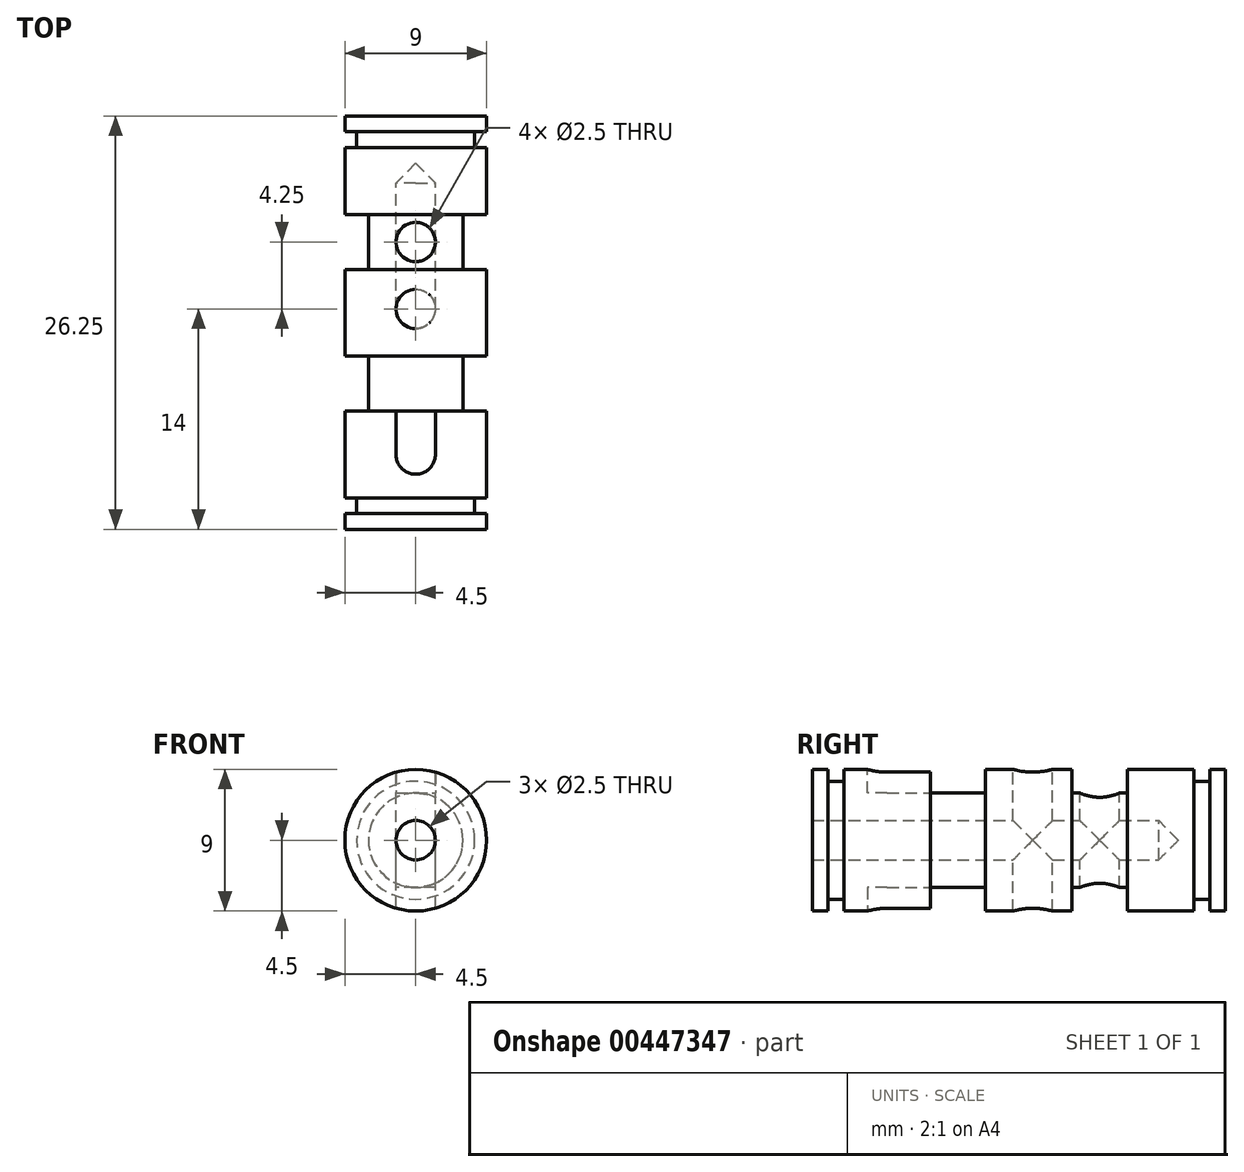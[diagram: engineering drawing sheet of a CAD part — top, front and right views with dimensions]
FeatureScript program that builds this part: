
annotation { "Feature Type Name" : "Feature", "Feature Type Description" : "" }
export const myFeature = defineFeature(function(context is Context, id is Id, definition is map)
    precondition{}
    {
        {
            var Q0;
            Q0=qCreatedBy(makeId("Top.planeOp"),FACE);
            var sketch = newSketch(context, id + "F0", { "sketchPlane" : qUnion([Q0])});
            skLineSegment(sketch, "E0", {"start": v(-2.5, 0) * mm, "end": v(-2.5, 0) * mm});
            skLineSegment(sketch, "E1", {"start": v(-2.5, 0) * mm, "end": v(-1.25, 0) * mm});
            skLineSegment(sketch, "E2", {"start": v(-1.25, 0) * mm, "end": v(-1.25, 22) * mm});
            skLineSegment(sketch, "E3", {"start": v(-1.25, 22) * mm, "end": v(0, 23.25) * mm});
            skLineSegment(sketch, "E4", {"start": v(0, 23.25) * mm, "end": v(0, 26.25) * mm});
            skLineSegment(sketch, "E5", {"start": v(0, 26.25) * mm, "end": v(-4.5, 26.25) * mm});
            skLineSegment(sketch, "E6", {"start": v(-4.5, 26.25) * mm, "end": v(-4.5, 25.25) * mm});
            skLineSegment(sketch, "E7", {"start": v(-4.5, 25.25) * mm, "end": v(-3.75, 25.25) * mm});
            skLineSegment(sketch, "E8", {"start": v(-3.75, 25.25) * mm, "end": v(-3.75, 24.25) * mm});
            skLineSegment(sketch, "E9", {"start": v(-3.75, 24.25) * mm, "end": v(-4.5, 24.25) * mm});
            skLineSegment(sketch, "E10", {"start": v(-4.5, 24.25) * mm, "end": v(-4.5, 20) * mm});
            skLineSegment(sketch, "E11", {"start": v(-4.5, 20) * mm, "end": v(-3, 20) * mm});
            skLineSegment(sketch, "E12", {"start": v(-3, 20) * mm, "end": v(-3, 16.5) * mm});
            skLineSegment(sketch, "E13", {"start": v(-3, 16.5) * mm, "end": v(-4.5, 16.5) * mm});
            skLineSegment(sketch, "E14", {"start": v(-4.5, 16.5) * mm, "end": v(-4.5, 11) * mm});
            skLineSegment(sketch, "E15", {"start": v(-4.5, 11) * mm, "end": v(-3, 11) * mm});
            skLineSegment(sketch, "E16", {"start": v(-3, 11) * mm, "end": v(-3, 7.5) * mm});
            skLineSegment(sketch, "E17", {"start": v(-3, 7.5) * mm, "end": v(-4.5, 7.5) * mm});
            skLineSegment(sketch, "E18", {"start": v(-4.5, 7.5) * mm, "end": v(-4.5, 2) * mm});
            skLineSegment(sketch, "E19", {"start": v(-4.5, 2) * mm, "end": v(-3.75, 2) * mm});
            skLineSegment(sketch, "E20", {"start": v(-3.75, 2) * mm, "end": v(-3.75, 1) * mm});
            skLineSegment(sketch, "E21", {"start": v(-3.75, 1) * mm, "end": v(-4.5, 1) * mm});
            skLineSegment(sketch, "E22", {"start": v(-4.5, 1) * mm, "end": v(-4.5, 0) * mm});
            skLineSegment(sketch, "E23", {"start": v(-4.5, 0) * mm, "end": v(-2.5, 0) * mm});
            skLineSegment(sketch, "E24", {"start": v(0, 9.96) * mm, "end": v(0, -5.2) * mm, "construction": true});
            skLineSegment(sketch, "E25", {"start": v(-3, 9.25) * mm, "end": v(-4.58, 9.25) * mm, "construction": true});
            skPoint(sketch, "E25.endSnap0", {"position": v(-3, 9.25) * mm});
            skLineSegment(sketch, "E26", {"start": v(-3, 18.25) * mm, "end": v(-4.58, 18.25) * mm, "construction": true});
            skLineSegment(sketch, "E27", {"start": v(-4.5, 13.75) * mm, "end": v(-1.25, 13.75) * mm, "construction": true});
            skLineSegment(sketch, "E28", {"start": v(-4.5, 4.75) * mm, "end": v(-1.25, 4.75) * mm, "construction": true});
            skPoint(sketch, "E28.endSnap0", {"position": v(-1.25, 11) * mm});
            skSolve(sketch);
        }
        {
            var Q0;
            Q0=makeQuery(id+"F0.imprint","IMPRINT",FACE,{"disambiguationData":[TD([[makeQuery(id+"F0.imprint","IMPRINT",EDGE,{"derivedFrom":sQuery(id+"F0.wireOp",EDGE,"E1")}),1.0]])]});
            var Q1;
            Q1=sQuery(id+"F0.wireOp",EDGE,"E24");
            revolve(context, id + "F1", {"entities" : qUnion([Q0]), "axis" : qUnion([Q1]), "revolveType" : RevolveType.FULL});
        }
        {
            var Q0;
            Q0=qCreatedBy(makeId("Top.planeOp"),FACE);
            cPlane(context, id + "F2", {"entities" : qUnion([Q0]), "cplaneType" : CPlaneType.OFFSET, "offset" : 4.5 * mm, "width" : 150 * mm, "height" : 150 * mm});
        }
        {
            var Q0;
            Q0=qCreatedBy(id+"F2.planeOp",FACE);
            var sketch = newSketch(context, id + "F3", { "sketchPlane" : qUnion([Q0])});
            skArc(sketch, "E29", {"start": v(-1.25, 4.75) * mm, "mid": v(0, 3.5) * mm, "end": v(1.25, 4.75) * mm});
            skLineSegment(sketch, "E30", {"start": v(-1.25, 4.75) * mm, "end": v(-1.25, 8.75) * mm});
            skLineSegment(sketch, "E31", {"start": v(1.25, 4.75) * mm, "end": v(1.25, 8.75) * mm});
            skLineSegment(sketch, "E32", {"start": v(1.25, 8.75) * mm, "end": v(-1.25, 8.75) * mm});
            skCircle(sketch, "E33", {"center": v(0, 14) * mm, "radius": 1.25 * mm});
            skCircle(sketch, "E34", {"center": v(0, 18.25) * mm, "radius": 1.25 * mm});
            skSolve(sketch);
        }
        {
            var Q0;
            Q0=makeQuery(id+"F3.imprint","IMPRINT",FACE,{"disambiguationData":[TD([[makeQuery(id+"F3.imprint","IMPRINT",EDGE,{"derivedFrom":sQuery(id+"F3.wireOp",EDGE,"E29")}),1.0]])]});
            extrude(context, id + "F4", {"entities" : qUnion([Q0]), "oppositeDirection" : true, "depth" : 1.5 * mm});
        }
        {
            var Q0;
            Q0=makeQuery(id+"F3.imprint","IMPRINT",FACE,{"disambiguationData":[TD([[makeQuery(id+"F3.imprint","IMPRINT",EDGE,{"derivedFrom":sQuery(id+"F3.wireOp",EDGE,"E33")}),1.0]])]});
            var Q1;
            Q1=makeQuery(id+"F3.imprint","IMPRINT",FACE,{"disambiguationData":[TD([[makeQuery(id+"F3.imprint","IMPRINT",EDGE,{"derivedFrom":sQuery(id+"F3.wireOp",EDGE,"E34")}),1.0]])]});
            extrude(context, id + "F5", {"entities" : qUnion([Q0, Q1]), "operationType" : NewBodyOperationType.REMOVE, "oppositeDirection" : true, "depth" : 25 * mm});
        }
        {
            var Q0;
            Q0=makeQuery(id+"F4.opExtrude","SWEPT_BODY",BODY,{"disambiguationData":[OSD([sQuery(id+"F3.wireOp",EDGE,"E29"),sQuery(id+"F3.wireOp",EDGE,"E30"),sQuery(id+"F3.wireOp",EDGE,"E31"),sQuery(id+"F3.wireOp",EDGE,"E32")])]});
            var Q1;
            Q1=makeQuery(id+"F1.opRevolve","SWEPT_EDGE",EDGE,{"disambiguationData":[OSD([sQuery(id+"F0.wireOp",EDGE,"E0"),sQuery(id+"F0.wireOp",EDGE,"E23")])]});
            circularPattern(context, id + "F6", {"entities" : qUnion([Q0]), "axis" : qUnion([Q1]), "angle" : 180 * degree, "instanceCount" : 2, "equalSpace" : true});
        }
        {
            var Q0;
            Q0=makeQuery(id+"F4.opExtrude","SWEPT_BODY",BODY,{"disambiguationData":[OSD([sQuery(id+"F3.wireOp",EDGE,"E29"),sQuery(id+"F3.wireOp",EDGE,"E30"),sQuery(id+"F3.wireOp",EDGE,"E31"),sQuery(id+"F3.wireOp",EDGE,"E32")])]});
            var Q1;
            Q1=makeQuery(id+"F6.opPattern","COPY",BODY,{"derivedFrom":makeQuery(id+"F4.opExtrude","SWEPT_BODY",BODY,{"disambiguationData":[OSD([sQuery(id+"F3.wireOp",EDGE,"E29"),sQuery(id+"F3.wireOp",EDGE,"E30"),sQuery(id+"F3.wireOp",EDGE,"E31"),sQuery(id+"F3.wireOp",EDGE,"E32")])]}),"instanceName":"1"});
            var Q2;
            Q2=makeQuery(id+"F1.opRevolve","SWEPT_BODY",BODY,{"disambiguationData":[OSD([sQuery(id+"F0.wireOp",EDGE,"E0"),sQuery(id+"F0.wireOp",EDGE,"E1"),sQuery(id+"F0.wireOp",EDGE,"E2"),sQuery(id+"F0.wireOp",EDGE,"E3"),sQuery(id+"F0.wireOp",EDGE,"E4"),sQuery(id+"F0.wireOp",EDGE,"E5"),sQuery(id+"F0.wireOp",EDGE,"E6"),sQuery(id+"F0.wireOp",EDGE,"E7"),sQuery(id+"F0.wireOp",EDGE,"E8"),sQuery(id+"F0.wireOp",EDGE,"E9"),sQuery(id+"F0.wireOp",EDGE,"E10"),sQuery(id+"F0.wireOp",EDGE,"E11"),sQuery(id+"F0.wireOp",EDGE,"E12"),sQuery(id+"F0.wireOp",EDGE,"E13"),sQuery(id+"F0.wireOp",EDGE,"E14"),sQuery(id+"F0.wireOp",EDGE,"E15"),sQuery(id+"F0.wireOp",EDGE,"E16"),sQuery(id+"F0.wireOp",EDGE,"E17"),sQuery(id+"F0.wireOp",EDGE,"E18"),sQuery(id+"F0.wireOp",EDGE,"E19"),sQuery(id+"F0.wireOp",EDGE,"E20"),sQuery(id+"F0.wireOp",EDGE,"E21"),sQuery(id+"F0.wireOp",EDGE,"E22"),sQuery(id+"F0.wireOp",EDGE,"E23")])]});
            booleanBodies(context, id + "F7", {"operationType" : BooleanOperationType.SUBTRACTION, "tools" : qUnion([Q0, Q1]), "targets" : qUnion([Q2])});
        }
    });
